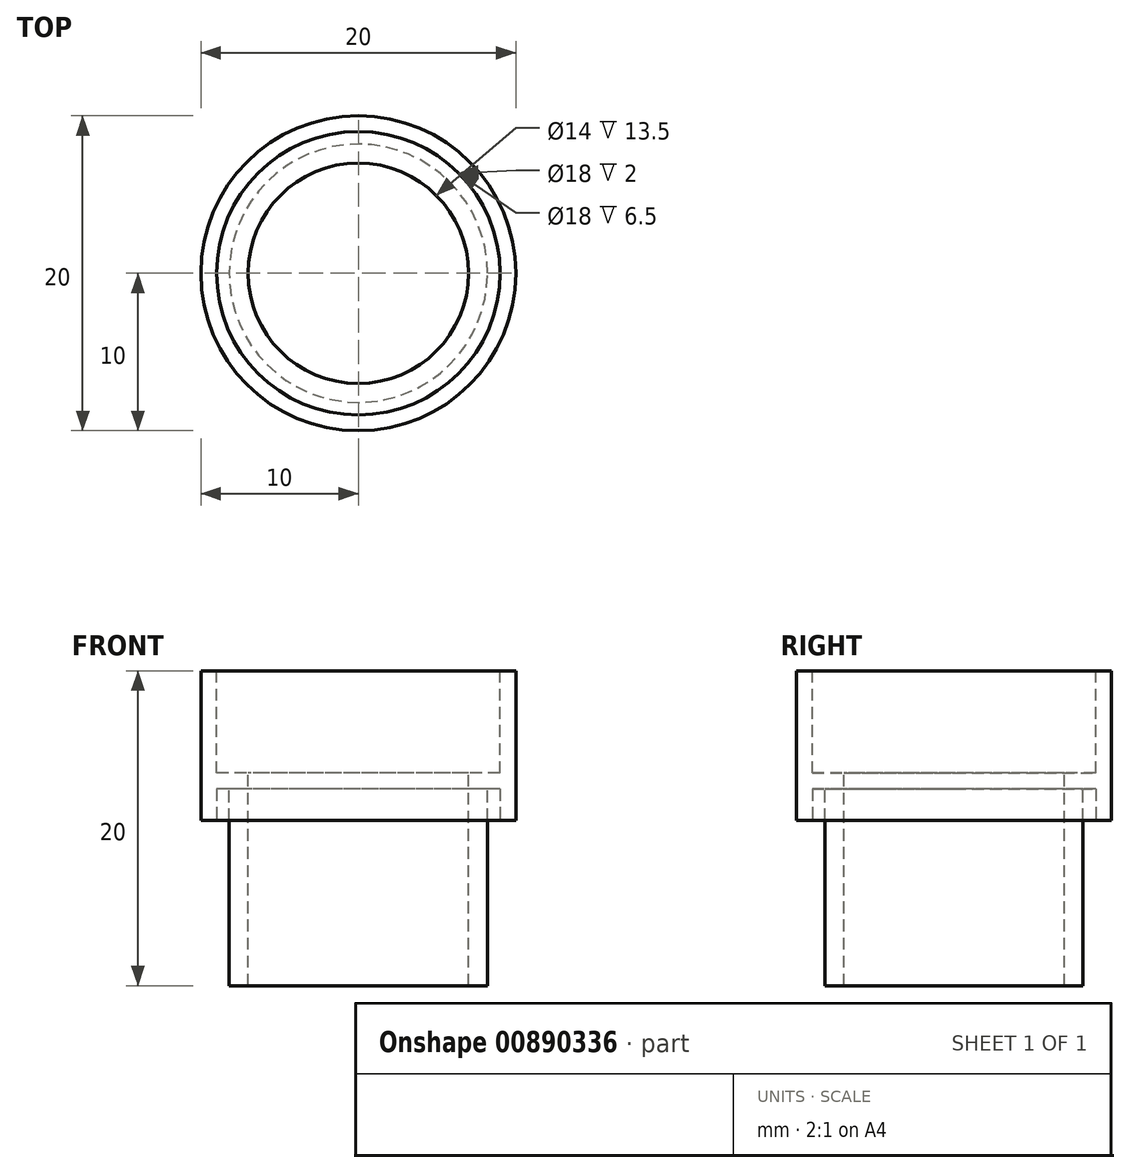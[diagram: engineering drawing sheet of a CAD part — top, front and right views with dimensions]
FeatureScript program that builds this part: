
annotation { "Feature Type Name" : "Feature", "Feature Type Description" : "" }
export const myFeature = defineFeature(function(context is Context, id is Id, definition is map)
    precondition{}
    {
        {
            var Q0;
            Q0=qCreatedBy(makeId("Top.planeOp"),FACE);
            var sketch = newSketch(context, id + "F0", { "sketchPlane" : qUnion([Q0])});
            skCircle(sketch, "E0", {"center": v(0, 0) * mm, "radius": 10 * mm});
            skCircle(sketch, "E1", {"center": v(0, 0) * mm, "radius": 9 * mm});
            skCircle(sketch, "E2", {"center": v(0, 0) * mm, "radius": 7 * mm});
            skCircle(sketch, "E3", {"center": v(0, 0) * mm, "radius": 8.2 * mm});
            skLineSegment(sketch, "E4", {"start": v(0, 7) * mm, "end": v(0, 8.2) * mm});
            skLineSegment(sketch, "E5", {"start": v(0, 8.2) * mm, "end": v(0, 9) * mm});
            skLineSegment(sketch, "E6", {"start": v(0, 9) * mm, "end": v(0, 10) * mm});
            skLineSegment(sketch, "E7", {"start": v(0, -7) * mm, "end": v(0, -8.2) * mm});
            skLineSegment(sketch, "E8", {"start": v(0, -8.2) * mm, "end": v(0, -9) * mm});
            skLineSegment(sketch, "E9", {"start": v(0, -9) * mm, "end": v(0, -10) * mm});
            skSolve(sketch);
        }
        {
            var Q0;
            {var subQ0=sQuery(id+"F0.wireOp",EDGE,"E6");Q0=makeQuery(id+"F0.imprint","IMPRINT",FACE,{"disambiguationData":[TD([[makeQuery(id+"F0.imprint","IMPRINT",EDGE,{"derivedFrom":subQ0}),1.0]])]});}
            extrude(context, id + "F1", {"entities" : qUnion([Q0]), "depth" : 2 * mm, "offsetDistance" : 25 * mm});
        }
        {
            var Q0;
            {var subQ0=sQuery(id+"F0.wireOp",EDGE,"E6");Q0=makeQuery(id+"F0.imprint","IMPRINT",FACE,{"disambiguationData":[TD([[makeQuery(id+"F0.imprint","IMPRINT",EDGE,{"derivedFrom":subQ0}),-1.0]])]});}
            var Q1;
            Q1 = qConstructionFilter(qBodyType(qCreatedBy(id + "F0" ,EDGE), BodyType.WIRE), ConstructionObject.NO);
            extrude(context, id + "F2", {"entities" : qUnion([Q0]), "operationType" : NewBodyOperationType.ADD, "surfaceEntities" : qUnion([Q1]), "depth" : 3 * mm, "offsetDistance" : 25 * mm});
        }
        {
            var Q0;
            Q0=makeQuery(id+"F1.opExtrude","CAP_FACE",FACE,{"disambiguationData":[OSD([sQuery(id+"F0.wireOp",EDGE,"E0"),sQuery(id+"F0.wireOp",EDGE,"E1")])],"isStart":false});
            var sketch = newSketch(context, id + "F3", { "sketchPlane" : qUnion([Q0])});
            skCircle(sketch, "E10", {"center": v(0, 0) * mm, "radius": 8.2 * mm});
            skCircle(sketch, "E11", {"center": v(0, 0) * mm, "radius": 10 * mm});
            skSolve(sketch);
        }
        {
            var Q0;
            Q0=makeQuery(id+"F3.imprint","IMPRINT",FACE,{"disambiguationData":[TD([[makeQuery(id+"F3.imprint","IMPRINT",EDGE,{"derivedFrom":sQuery(id+"F3.wireOp",EDGE,"E11")}),1.0]])]});
            var Q1;
            Q1=makeQuery(id+"F3.imprint","IMPRINT",FACE,{"disambiguationData":[TD([[makeQuery(id+"F3.imprint","IMPRINT",EDGE,{"derivedFrom":sQuery(id+"F3.wireOp",EDGE,"E10")}),-1.0]])]});
            extrude(context, id + "F4", {"entities" : qUnion([Q0, Q1]), "operationType" : NewBodyOperationType.ADD, "depth" : 7.5 * mm, "offsetDistance" : 25 * mm});
        }
        {
            var Q0;
            Q0=makeQuery(id+"F4.opExtrude","CAP_FACE",FACE,{"disambiguationData":[OSD([sQuery(id+"F3.wireOp",EDGE,"E10"),sQuery(id+"F3.wireOp",EDGE,"E11")])],"isStart":false});
            var sketch = newSketch(context, id + "F5", { "sketchPlane" : qUnion([Q0])});
            skCircle(sketch, "E12", {"center": v(0, 0) * mm, "radius": 7 * mm});
            skSolve(sketch);
        }
        {
            var Q0;
            Q0=makeQuery(id+"F5.imprint","IMPRINT",FACE,{"disambiguationData":[TD([[makeQuery(id+"F5.imprint","IMPRINT",EDGE,{"derivedFrom":sQuery(id+"F5.wireOp",EDGE,"E12")}),-1.0]])]});
            extrude(context, id + "F6", {"entities" : qUnion([Q0]), "operationType" : NewBodyOperationType.ADD, "oppositeDirection" : true, "depth" : 20 * mm, "offsetDistance" : 25 * mm});
        }
        {
            var Q0;
            {var subQ0=sQuery(id+"F3.wireOp",EDGE,"E10");Q0=makeQuery(id+"F6.boolean.opBoolean","MERGE",FACE,{"derivedFrom":[makeQuery(id+"F4.opExtrude","CAP_FACE",FACE,{"disambiguationData":[OSD([subQ0,sQuery(id+"F3.wireOp",EDGE,"E11")])],"isStart":false}),makeQuery(id+"F6.opExtrude","CAP_FACE",FACE,{"disambiguationData":[OSD([subQ0,sQuery(id+"F5.wireOp",EDGE,"E12")])],"isStart":true})]});}
            var sketch = newSketch(context, id + "F7", { "sketchPlane" : qUnion([Q0])});
            skCircle(sketch, "E13", {"center": v(0, 0) * mm, "radius": 9 * mm});
            skCircle(sketch, "E14", {"center": v(0, 0) * mm, "radius": 7 * mm});
            skSolve(sketch);
        }
        {
            var Q0;
            Q0 = qSketchRegion(id + "F7", true);
            extrude(context, id + "F8", {"entities" : qUnion([Q0]), "operationType" : NewBodyOperationType.REMOVE, "oppositeDirection" : true, "depth" : 6.5 * mm, "offsetDistance" : 25 * mm});
        }
    });
